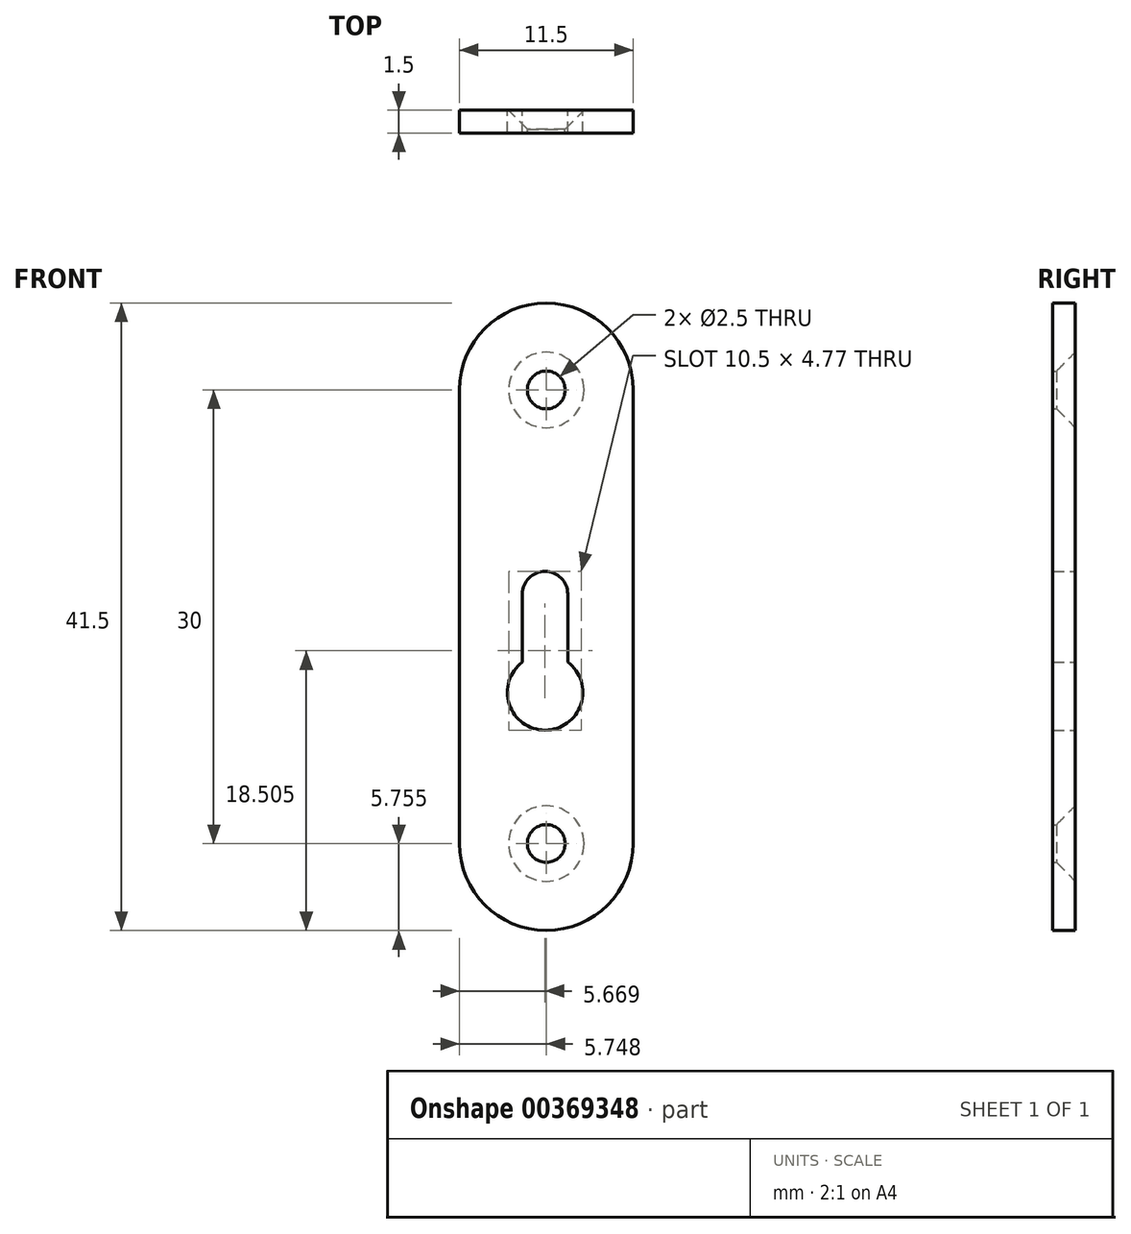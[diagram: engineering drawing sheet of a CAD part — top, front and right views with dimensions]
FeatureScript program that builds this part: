
annotation { "Feature Type Name" : "Feature", "Feature Type Description" : "" }
export const myFeature = defineFeature(function(context is Context, id is Id, definition is map)
    precondition{}
    {
        {
            var Q0;
            Q0=qCreatedBy(makeId("Front.planeOp"),FACE);
            var sketch = newSketch(context, id + "F0", { "sketchPlane" : qUnion([Q0])});
            skLineSegment(sketch, "E0.bottom", {"start": v(-15.31, 37.84) * mm, "end": v(-3.81, 37.84) * mm});
            skLineSegment(sketch, "E0.top", {"start": v(-15.31, 7.84) * mm, "end": v(-3.81, 7.84) * mm});
            skLineSegment(sketch, "E0.left", {"start": v(-15.31, 37.84) * mm, "end": v(-15.31, 7.84) * mm});
            skLineSegment(sketch, "E0.right", {"start": v(-3.81, 37.84) * mm, "end": v(-3.81, 7.84) * mm});
            skArc(sketch, "E1", {"start": v(-3.81, 37.84) * mm, "mid": v(-9.56, 43.6) * mm, "end": v(-15.31, 37.84) * mm});
            skArc(sketch, "E2", {"start": v(-15.31, 7.84) * mm, "mid": v(-9.56, 2.1) * mm, "end": v(-3.81, 7.84) * mm});
            skSolve(sketch);
        }
        {
            var Q0;
            Q0=makeQuery(id+"F0.imprint","IMPRINT",FACE,{"disambiguationData":[TD([[makeQuery(id+"F0.imprint","IMPRINT",EDGE,{"derivedFrom":sQuery(id+"F0.wireOp",EDGE,"E0.bottom")}),1.0]])]});
            var Q1;
            Q1=makeQuery(id+"F0.imprint","IMPRINT",FACE,{"disambiguationData":[TD([[makeQuery(id+"F0.imprint","IMPRINT",EDGE,{"derivedFrom":sQuery(id+"F0.wireOp",EDGE,"E0.bottom")}),-1.0]])]});
            var Q2;
            Q2=makeQuery(id+"F0.imprint","IMPRINT",FACE,{"disambiguationData":[TD([[makeQuery(id+"F0.imprint","IMPRINT",EDGE,{"derivedFrom":sQuery(id+"F0.wireOp",EDGE,"E0.top")}),-1.0]])]});
            extrude(context, id + "F1", {"entities" : qUnion([Q0, Q1, Q2]), "depth" : 1.5 * mm});
        }
        {
            var Q0;
            Q0=sQuery(id+"F0.wireOp",VERTEX,"E1.center");
            var Q1;
            Q1=sQuery(id+"F0.wireOp",VERTEX,"E2.center");
            var Q2;
            Q2=makeQuery(id+"F1.opExtrude","SWEPT_BODY",BODY,{"disambiguationData":[OSD([sQuery(id+"F0.wireOp",EDGE,"E0.left"),sQuery(id+"F0.wireOp",EDGE,"E0.right"),sQuery(id+"F0.wireOp",EDGE,"E1"),sQuery(id+"F0.wireOp",EDGE,"E2")])]});
            hole(context, id + "F2", {"style" : HoleStyle.C_SINK, "endStyle" : HoleEndStyle.THROUGH, "oppositeDirection" : true, "standardTappedOrClearance" : lookupTablePath({ "standard" : "ISO", "size" : "2.5", "type" : "Drilled" }), "standardBlindInLast" : lookupTablePath({ "standard" : "ISO", "size" : "2.5", "type" : "Drilled" }), "holeDiameter" : 2.5 * mm, "cSinkDiameter" : 5 * mm, "cSinkAngle" : 90 * degree, "isTappedThrough" : true, "tappedDepth" : 12 * mm, "tapClearance" : 3, "locations" : qUnion([Q0, Q1]), "scope" : qUnion([Q2])});
        }
        {
            var Q0;
            Q0=makeQuery(id+"F0.imprint","IMPRINT",FACE,{"disambiguationData":[TD([[makeQuery(id+"F0.imprint","IMPRINT",EDGE,{"derivedFrom":sQuery(id+"F0.wireOp",EDGE,"E0.bottom")}),-1.0]])]});
            var sketch = newSketch(context, id + "F3", { "sketchPlane" : qUnion([Q0])});
            skLineSegment(sketch, "E3.bottom", {"start": v(-8.14, 25.84) * mm, "end": v(-11.14, 25.84) * mm});
            skLineSegment(sketch, "E3.top", {"start": v(-8.14, 17.84) * mm, "end": v(-11.14, 17.84) * mm});
            skLineSegment(sketch, "E3.left", {"start": v(-8.14, 25.84) * mm, "end": v(-8.14, 17.84) * mm});
            skLineSegment(sketch, "E3.right", {"start": v(-11.14, 25.84) * mm, "end": v(-11.14, 17.84) * mm});
            skCircle(sketch, "E4", {"center": v(-9.64, 17.84) * mm, "radius": 2.5 * mm});
            skSolve(sketch);
        }
        {
            var Q0;
            Q0 = qSketchRegion(id + "F3", true);
            extrude(context, id + "F4", {"entities" : qUnion([Q0]), "operationType" : NewBodyOperationType.REMOVE, "depth" : 25 * mm});
        }
        {
            var Q0;
            Q0=makeQuery(id+"F4.boolean.opBoolean","COPY",EDGE,{"derivedFrom":makeQuery(id+"F4.opExtrude","SWEPT_EDGE",EDGE,{"disambiguationData":[OSD([sQuery(id+"F3.wireOp",EDGE,"E3.bottom"),sQuery(id+"F3.wireOp",EDGE,"E3.left")])]})});
            var Q1;
            Q1=makeQuery(id+"F4.boolean.opBoolean","COPY",EDGE,{"derivedFrom":makeQuery(id+"F4.opExtrude","SWEPT_EDGE",EDGE,{"disambiguationData":[OSD([sQuery(id+"F3.wireOp",EDGE,"E3.bottom"),sQuery(id+"F3.wireOp",EDGE,"E3.right")])]})});
            fillet(context, id + "F5", {"entities" : qUnion([Q0, Q1]), "radius" : 1.5 * mm, "tangentPropagation" : true, "allowEdgeOverflow" : false});
        }
    });
